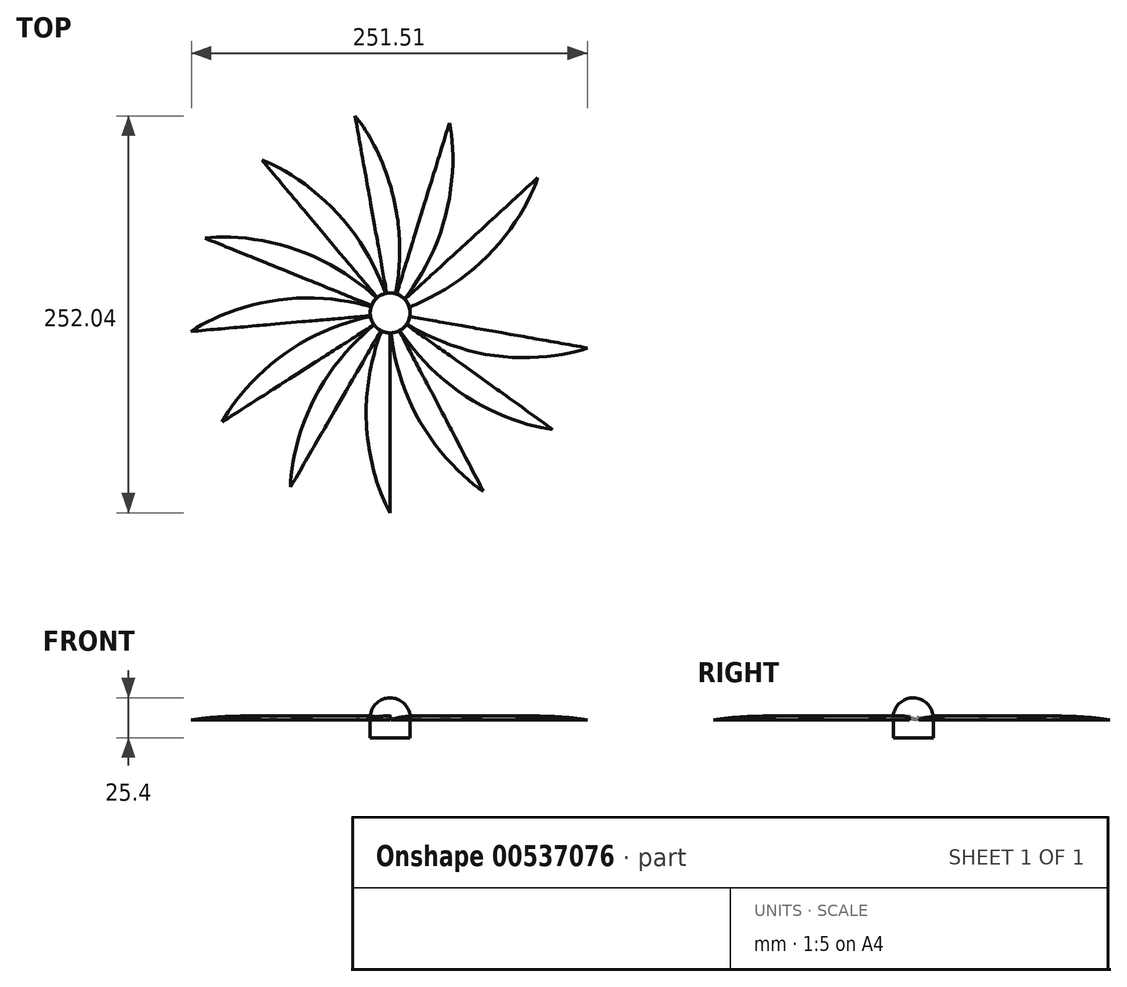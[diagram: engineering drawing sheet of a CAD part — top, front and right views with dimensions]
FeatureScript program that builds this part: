
annotation { "Feature Type Name" : "Feature", "Feature Type Description" : "" }
export const myFeature = defineFeature(function(context is Context, id is Id, definition is map)
    precondition{}
    {
        {
            var Q0;
            Q0=qCreatedBy(makeId("Top.planeOp"),FACE);
            var sketch = newSketch(context, id + "F0", { "sketchPlane" : qUnion([Q0])});
            skCircle(sketch, "E0", {"center": v(0, 0) * mm, "radius": 12.7 * mm});
            skLineSegment(sketch, "E1", {"start": v(0, 0) * mm, "end": v(0, 12.7) * mm});
            skLineSegment(sketch, "E2", {"start": v(0, 0) * mm, "end": v(0, -12.7) * mm});
            skSolve(sketch);
        }
        {
            var Q0;
            {var subQ0=sQuery(id+"F0.wireOp",EDGE,"E1");Q0=makeQuery(id+"F0.imprint","IMPRINT",FACE,{"disambiguationData":[TD([[makeQuery(id+"F0.imprint","IMPRINT",EDGE,{"derivedFrom":subQ0}),-1.0]])]});}
            var Q1;
            Q1=sQuery(id+"F0.wireOp",EDGE,"E1");
            revolve(context, id + "F1", {"entities" : qUnion([Q0]), "axis" : qUnion([Q1]), "revolveType" : RevolveType.FULL});
        }
        {
            var Q0;
            Q0=qCreatedBy(makeId("Top.planeOp"),FACE);
            var sketch = newSketch(context, id + "F2", { "sketchPlane" : qUnion([Q0])});
            skLineSegment(sketch, "E3", {"start": v(0, 0) * mm, "end": v(0, -127) * mm});
            skLineSegment(sketch, "E4", {"start": v(0, 0) * mm, "end": v(0, -63.5) * mm});
            skLineSegment(sketch, "E5", {"start": v(0, 63.5) * mm, "end": v(15.24, 63.5) * mm});
            skLineSegment(sketch, "E6", {"start": v(0, -63.5) * mm, "end": v(-15.24, -63.5) * mm});
            skFitSpline(sketch, "E7", {"points": [v(0, 0) * mm, v(-15.24, -63.5) * mm, v(0, -127) * mm], "startDerivative": vector(-45.72, -76.2) * mm, "endDerivative": vector(45.72, -76.2) * mm});
            skLineSegment(sketch, "E8", {"start": v(0.24, -0.68) * mm, "end": v(59.19, -113.17) * mm});
            skLineSegment(sketch, "E9", {"start": v(0.24, -0.68) * mm, "end": v(29.72, -56.92) * mm});
            skFitSpline(sketch, "E10", {"points": [v(0.24, -0.68) * mm, v(16.22, -64) * mm, v(59.19, -113.17) * mm], "startDerivative": vector(-5.13, -88.72) * mm, "endDerivative": vector(75.86, -46.28) * mm});
            skLineSegment(sketch, "E11", {"start": v(0, 0) * mm, "end": v(103.27, -73.92) * mm});
            skLineSegment(sketch, "E12", {"start": v(0, 0) * mm, "end": v(51.64, -36.96) * mm});
            skFitSpline(sketch, "E13", {"points": [v(0, 0) * mm, v(42.77, -49.35) * mm, v(103.27, -73.92) * mm], "startDerivative": vector(35.35, -81.53) * mm, "endDerivative": vector(88.57, -7.17) * mm});
            skLineSegment(sketch, "E14", {"start": v(0.17, -0.17) * mm, "end": v(125.24, -22.22) * mm});
            skLineSegment(sketch, "E15", {"start": v(0.17, -0.17) * mm, "end": v(62.7, -11.2) * mm});
            skFitSpline(sketch, "E16", {"points": [v(0.17, -0.17) * mm, v(60.06, -26.2) * mm, v(125.24, -22.22) * mm], "startDerivative": vector(70.33, -52.99) * mm, "endDerivative": vector(82.98, 31.8) * mm});
            skLineSegment(sketch, "E17", {"start": v(0.17, -0.17) * mm, "end": v(121.45, 37.53) * mm});
            skFitSpline(sketch, "E18", {"points": [v(0.17, -0.17) * mm, v(65.33, 4.13) * mm, v(121.45, 37.53) * mm], "startDerivative": vector(86.34, -21.04) * mm, "endDerivative": vector(59.2, 66.28) * mm});
            skLineSegment(sketch, "E19", {"start": v(0, 0) * mm, "end": v(93.62, 85.82) * mm});
            skFitSpline(sketch, "E20", {"points": [v(0, 0) * mm, v(57.1, 31.67) * mm, v(93.62, 85.82) * mm], "startDerivative": vector(87.07, 17.79) * mm, "endDerivative": vector(25.28, 85.2) * mm});
            skLineSegment(sketch, "E21", {"start": v(0.24, -0.68) * mm, "end": v(37.6, 120.7) * mm});
            skFitSpline(sketch, "E22", {"points": [v(0.24, -0.68) * mm, v(33.49, 55.53) * mm, v(37.6, 120.7) * mm], "startDerivative": vector(66.11, 59.38) * mm, "endDerivative": vector(-21.28, 86.28) * mm});
            skLineSegment(sketch, "E23", {"start": v(0, 0) * mm, "end": v(-22.24, 125.04) * mm});
            skFitSpline(sketch, "E24", {"points": [v(0, 0) * mm, v(3.88, 65.19) * mm, v(-22.24, 125.04) * mm], "startDerivative": vector(31.67, 83.03) * mm, "endDerivative": vector(-58.36, 67.01) * mm});
            skLineSegment(sketch, "E25", {"start": v(0.17, -0.17) * mm, "end": v(-81.46, 97.12) * mm});
            skFitSpline(sketch, "E26", {"points": [v(0.17, -0.17) * mm, v(-28.97, 58.27) * mm, v(-81.46, 97.12) * mm], "startDerivative": vector(-13.96, 87.76) * mm, "endDerivative": vector(-84, 28.98) * mm});
            skLineSegment(sketch, "E27", {"start": v(0.17, -0.17) * mm, "end": v(-117.57, 47.45) * mm});
            skFitSpline(sketch, "E28", {"points": [v(0.17, -0.17) * mm, v(-52.98, 37.77) * mm, v(-117.57, 47.45) * mm], "startDerivative": vector(-53.5, 70.96) * mm, "endDerivative": vector(-87.78, -13.81) * mm});
            skLineSegment(sketch, "E29", {"start": v(0.24, -0.68) * mm, "end": v(-126.27, -11.74) * mm});
            skFitSpline(sketch, "E30", {"points": [v(0.24, -0.68) * mm, v(-64.34, 8.97) * mm, v(-126.27, -11.74) * mm], "startDerivative": vector(-79.9, 38.9) * mm, "endDerivative": vector(-71.93, -52.19) * mm});
            skLineSegment(sketch, "E31", {"start": v(0.24, -0.68) * mm, "end": v(-106.62, -69.3) * mm});
            skFitSpline(sketch, "E32", {"points": [v(0.24, -0.68) * mm, v(-61.42, -22.16) * mm, v(-106.62, -69.3) * mm], "startDerivative": vector(-88.82, -2.7) * mm, "endDerivative": vector(-39.42, -79.64) * mm});
            skLineSegment(sketch, "E33", {"start": v(0.24, -0.68) * mm, "end": v(-63.26, -110.66) * mm});
            skFitSpline(sketch, "E34", {"points": [v(0.24, -0.68) * mm, v(-44.7, -48.05) * mm, v(-63.26, -110.66) * mm], "startDerivative": vector(-77.7, -43.13) * mm, "endDerivative": vector(1.5, -88.85) * mm});
            skSolve(sketch);
        }
        {
            var Q0;
            {var subQ0=sQuery(id+"F2.wireOp",EDGE,"E4");Q0=makeQuery(id+"F2.imprint","IMPRINT",FACE,{"disambiguationData":[TD([[makeQuery(id+"F2.imprint","IMPRINT",EDGE,{"derivedFrom":subQ0}),-1.0]])]});}
            var Q1;
            {var subQ0=sQuery(id+"F2.wireOp",EDGE,"E3");Q1=makeQuery(id+"F2.imprint","IMPRINT",FACE,{"disambiguationData":[TD([[makeQuery(id+"F2.imprint","IMPRINT",EDGE,{"derivedFrom":subQ0}),-1.0]])]});}
            var Q2;
            {var subQ0=sQuery(id+"F2.wireOp",EDGE,"19Io6KP2-8sqI-wjnz-AJ6c-VTp4O6TYuGnM");Q2=makeQuery(id+"F2.imprint","IMPRINT",FACE,{"disambiguationData":[TD([[makeQuery(id+"F2.imprint","IMPRINT",EDGE,{"derivedFrom":subQ0}),-1.0]])]});}
            var Q3;
            {var subQ0=sQuery(id+"F2.wireOp",EDGE,"X4IT270C-a7Zd-RReP-n4iX-xOcwQeBmdPC1");Q3=makeQuery(id+"F2.imprint","IMPRINT",FACE,{"disambiguationData":[TD([[makeQuery(id+"F2.imprint","IMPRINT",EDGE,{"derivedFrom":subQ0}),-1.0]])]});}
            var Q4;
            {var subQ0=sQuery(id+"F2.wireOp",EDGE,"E6");Q4=makeQuery(id+"F2.imprint","IMPRINT",FACE,{"disambiguationData":[TD([[makeQuery(id+"F2.imprint","IMPRINT",EDGE,{"derivedFrom":subQ0}),-1.0]])]});}
            var Q5;
            {var subQ0=sQuery(id+"F2.wireOp",EDGE,"E33");var subQ1=sQuery(id+"F2.wireOp",EDGE,"E7");var subQ2=makeQuery(id+"F2.imprint","INTERSECT",VERTEX,{"derivedFrom":[subQ1,subQ0]});Q5=makeQuery(id+"F2.imprint","IMPRINT",FACE,{"disambiguationData":[TD([[makeQuery(id+"F2.imprint","IMPRINT",EDGE,{"disambiguationData":[TD([[subQ2,1.0]])],"derivedFrom":subQ1}),-1.0]])]});}
            var Q6;
            {var subQ3=sQuery(id+"F2.wireOp",EDGE,"E29");var subQ7=sQuery(id+"F2.wireOp",EDGE,"E7");var subQ8=makeQuery(id+"F2.imprint","INTERSECT",VERTEX,{"derivedFrom":[subQ7,subQ3]});Q6=makeQuery(id+"F2.imprint","IMPRINT",FACE,{"disambiguationData":[TD([[makeQuery(id+"F2.imprint","IMPRINT",EDGE,{"disambiguationData":[TD([[subQ8,-1.0]])],"derivedFrom":subQ7}),-1.0]])]});}
            var Q7;
            {var subQ0=sQuery(id+"F2.wireOp",EDGE,"E30");var subQ1=sQuery(id+"F2.wireOp",EDGE,"E7");var subQ2=makeQuery(id+"F2.imprint","INTERSECT",VERTEX,{"derivedFrom":[subQ1,subQ0]});Q7=makeQuery(id+"F2.imprint","IMPRINT",FACE,{"disambiguationData":[TD([[makeQuery(id+"F2.imprint","IMPRINT",EDGE,{"disambiguationData":[TD([[subQ2,-1.0]])],"derivedFrom":subQ1}),-1.0]])]});}
            var Q8;
            {var subQ0=sQuery(id+"F2.wireOp",EDGE,"E28");var subQ5=sQuery(id+"F2.wireOp",EDGE,"E25");var subQ6=makeQuery(id+"F2.imprint","INTERSECT",VERTEX,{"derivedFrom":[subQ5,subQ0]});Q8=makeQuery(id+"F2.imprint","IMPRINT",FACE,{"disambiguationData":[TD([[makeQuery(id+"F2.imprint","IMPRINT",EDGE,{"disambiguationData":[TD([[subQ6,1.0]])],"derivedFrom":subQ5}),1.0]])]});}
            var Q9;
            {var subQ0=sQuery(id+"F2.wireOp",EDGE,"E26");var subQ1=sQuery(id+"F2.wireOp",EDGE,"E23");var subQ2=makeQuery(id+"F2.imprint","INTERSECT",VERTEX,{"derivedFrom":[subQ1,subQ0]});Q9=makeQuery(id+"F2.imprint","IMPRINT",FACE,{"disambiguationData":[TD([[makeQuery(id+"F2.imprint","IMPRINT",EDGE,{"disambiguationData":[TD([[subQ2,1.0]])],"derivedFrom":subQ1}),1.0]])]});}
            var Q10;
            {var subQ0=sQuery(id+"F2.wireOp",EDGE,"E24");var subQ1=sQuery(id+"F2.wireOp",EDGE,"E23");var subQ2=makeQuery(id+"F2.imprint","INTERSECT",VERTEX,{"derivedFrom":[subQ1,subQ0]});Q10=makeQuery(id+"F2.imprint","IMPRINT",FACE,{"disambiguationData":[TD([[makeQuery(id+"F2.imprint","IMPRINT",EDGE,{"disambiguationData":[TD([[subQ2,1.0]])],"derivedFrom":subQ1}),-1.0]])]});}
            var Q11;
            {var subQ0=sQuery(id+"F2.wireOp",EDGE,"E21");var subQ1=sQuery(id+"F2.wireOp",EDGE,"E19");var subQ2=makeQuery(id+"F2.imprint","INTERSECT",VERTEX,{"derivedFrom":[subQ1,subQ0]});Q11=makeQuery(id+"F2.imprint","IMPRINT",FACE,{"disambiguationData":[TD([[makeQuery(id+"F2.imprint","IMPRINT",EDGE,{"disambiguationData":[TD([[subQ2,-1.0]])],"derivedFrom":subQ1}),1.0]])]});}
            var Q12;
            {var subQ0=sQuery(id+"F2.wireOp",EDGE,"E20");var subQ1=sQuery(id+"F2.wireOp",EDGE,"E17");var subQ8=makeQuery(id+"F2.imprint","INTERSECT",VERTEX,{"disambiguationData":[OD(0.0)],"derivedFrom":[subQ1,subQ0]});Q12=makeQuery(id+"F2.imprint","IMPRINT",FACE,{"disambiguationData":[TD([[makeQuery(id+"F2.imprint","IMPRINT",EDGE,{"disambiguationData":[TD([[subQ8,1.0]])],"derivedFrom":subQ1}),1.0]])]});}
            var Q13;
            {var subQ0=sQuery(id+"F2.wireOp",EDGE,"E18");var subQ3=sQuery(id+"F2.wireOp",EDGE,"E15");var subQ4=makeQuery(id+"F2.imprint","INTERSECT",VERTEX,{"derivedFrom":[subQ3,subQ0]});Q13=makeQuery(id+"F2.imprint","IMPRINT",FACE,{"disambiguationData":[TD([[makeQuery(id+"F2.imprint","IMPRINT",EDGE,{"disambiguationData":[TD([[subQ4,1.0]])],"derivedFrom":subQ3}),1.0]])]});}
            var Q14;
            {var subQ1=sQuery(id+"F2.wireOp",EDGE,"E14");Q14=makeQuery(id+"F2.imprint","IMPRINT",FACE,{"disambiguationData":[TD([[makeQuery(id+"F2.imprint","IMPRINT",EDGE,{"derivedFrom":subQ1}),-1.0]])]});}
            var Q15;
            {var subQ9=sQuery(id+"F2.wireOp",EDGE,"E11");Q15=makeQuery(id+"F2.imprint","IMPRINT",FACE,{"disambiguationData":[TD([[makeQuery(id+"F2.imprint","IMPRINT",EDGE,{"derivedFrom":subQ9}),-1.0]])]});}
            var Q16;
            {var subQ2=sQuery(id+"F2.wireOp",EDGE,"E8");Q16=makeQuery(id+"F2.imprint","IMPRINT",FACE,{"disambiguationData":[TD([[makeQuery(id+"F2.imprint","IMPRINT",EDGE,{"derivedFrom":subQ2}),-1.0]])]});}
            extrude(context, id + "F3", {"entities" : qUnion([Q0, Q1, Q2, Q3, Q4, Q5, Q6, Q7, Q8, Q9, Q10, Q11, Q12, Q13, Q14, Q15, Q16]), "operationType" : NewBodyOperationType.ADD, "depth" : 2.54 * mm, "offsetDistance" : 25.4 * mm, "symmetric" : true});
        }
        {
            var Q0;
            Q0=makeQuery(id+"F3.opExtrude","CAP_EDGE",EDGE,{"disambiguationData":[OSD([sQuery(id+"F2.wireOp",EDGE,"0b77368a-5ada-40fb-88a0-015b6c9d9cfb")])],"isStart":false});
            var Q1;
            Q1=makeQuery(id+"F3.opExtrude","CAP_EDGE",EDGE,{"disambiguationData":[OSD([sQuery(id+"F2.wireOp",EDGE,"E7")])],"isStart":false});
            var Q2;
            {var subQ0=sQuery(id+"F2.wireOp",EDGE,"E34");Q2=makeQuery(id+"F3.opExtrude","CAP_EDGE",EDGE,{"disambiguationData":[OSD([subQ0]),TDD([makeQuery(id+"F2.imprint","IMPRINT",EDGE,{"disambiguationData":[TD([[makeQuery(id+"F2.imprint","INTERSECT",VERTEX,{"derivedFrom":[sQuery(id+"F2.wireOp",EDGE,"E33"),subQ0]}),1.0]])],"derivedFrom":subQ0})])],"isStart":false});}
            var Q3;
            {var subQ0=sQuery(id+"F2.wireOp",EDGE,"E32");Q3=makeQuery(id+"F3.opExtrude","CAP_EDGE",EDGE,{"disambiguationData":[OSD([subQ0]),TDD([makeQuery(id+"F2.imprint","IMPRINT",EDGE,{"disambiguationData":[TD([[makeQuery(id+"F2.imprint","INTERSECT",VERTEX,{"derivedFrom":[sQuery(id+"F2.wireOp",EDGE,"E31"),subQ0]}),1.0]])],"derivedFrom":subQ0})])],"isStart":false});}
            var Q4;
            Q4=makeQuery(id+"F3.opExtrude","CAP_EDGE",EDGE,{"disambiguationData":[OSD([sQuery(id+"F2.wireOp",EDGE,"E30")])],"isStart":false});
            var Q5;
            {var subQ0=sQuery(id+"F2.wireOp",EDGE,"E28");Q5=makeQuery(id+"F3.opExtrude","CAP_EDGE",EDGE,{"disambiguationData":[OSD([subQ0]),TDD([makeQuery(id+"F2.imprint","IMPRINT",EDGE,{"disambiguationData":[TD([[makeQuery(id+"F2.imprint","INTERSECT",VERTEX,{"derivedFrom":[sQuery(id+"F2.wireOp",EDGE,"E27"),subQ0]}),1.0]])],"derivedFrom":subQ0})])],"isStart":false});}
            var Q6;
            {var subQ0=sQuery(id+"F2.wireOp",EDGE,"E26");Q6=makeQuery(id+"F3.opExtrude","CAP_EDGE",EDGE,{"disambiguationData":[OSD([subQ0]),TDD([makeQuery(id+"F2.imprint","IMPRINT",EDGE,{"disambiguationData":[TD([[makeQuery(id+"F2.imprint","INTERSECT",VERTEX,{"derivedFrom":[sQuery(id+"F2.wireOp",EDGE,"E25"),subQ0]}),1.0]])],"derivedFrom":subQ0})])],"isStart":false});}
            var Q7;
            Q7=makeQuery(id+"F3.opExtrude","CAP_EDGE",EDGE,{"disambiguationData":[OSD([sQuery(id+"F2.wireOp",EDGE,"E24")])],"isStart":false});
            var Q8;
            {var subQ0=sQuery(id+"F2.wireOp",EDGE,"E22");Q8=makeQuery(id+"F3.opExtrude","CAP_EDGE",EDGE,{"disambiguationData":[OSD([subQ0]),TDD([makeQuery(id+"F2.imprint","IMPRINT",EDGE,{"disambiguationData":[TD([[makeQuery(id+"F2.imprint","INTERSECT",VERTEX,{"derivedFrom":[sQuery(id+"F2.wireOp",EDGE,"E21"),subQ0]}),1.0]])],"derivedFrom":subQ0})])],"isStart":false});}
            var Q9;
            {var subQ0=sQuery(id+"F2.wireOp",EDGE,"E20");Q9=makeQuery(id+"F3.opExtrude","CAP_EDGE",EDGE,{"disambiguationData":[OSD([subQ0]),TDD([makeQuery(id+"F2.imprint","IMPRINT",EDGE,{"disambiguationData":[TD([[makeQuery(id+"F2.imprint","INTERSECT",VERTEX,{"derivedFrom":[sQuery(id+"F2.wireOp",EDGE,"E19"),subQ0]}),1.0]])],"derivedFrom":subQ0})])],"isStart":false});}
            var Q10;
            {var subQ0=sQuery(id+"F2.wireOp",EDGE,"E18");Q10=makeQuery(id+"F3.opExtrude","CAP_EDGE",EDGE,{"disambiguationData":[OSD([subQ0]),TDD([makeQuery(id+"F2.imprint","IMPRINT",EDGE,{"disambiguationData":[TD([[makeQuery(id+"F2.imprint","INTERSECT",VERTEX,{"derivedFrom":[sQuery(id+"F2.wireOp",EDGE,"E17"),subQ0]}),1.0]])],"derivedFrom":subQ0})])],"isStart":false});}
            var Q11;
            {var subQ0=sQuery(id+"F2.wireOp",EDGE,"E16");Q11=makeQuery(id+"F3.opExtrude","CAP_EDGE",EDGE,{"disambiguationData":[OSD([subQ0]),TDD([makeQuery(id+"F2.imprint","IMPRINT",EDGE,{"disambiguationData":[TD([[makeQuery(id+"F2.imprint","INTERSECT",VERTEX,{"derivedFrom":[sQuery(id+"F2.wireOp",EDGE,"E14"),subQ0]}),1.0]])],"derivedFrom":subQ0})])],"isStart":false});}
            var Q12;
            {var subQ0=sQuery(id+"F2.wireOp",EDGE,"E13");Q12=makeQuery(id+"F3.opExtrude","CAP_EDGE",EDGE,{"disambiguationData":[OSD([subQ0]),TDD([makeQuery(id+"F2.imprint","IMPRINT",EDGE,{"disambiguationData":[TD([[makeQuery(id+"F2.imprint","INTERSECT",VERTEX,{"derivedFrom":[sQuery(id+"F2.wireOp",EDGE,"E11"),subQ0]}),1.0]])],"derivedFrom":subQ0})])],"isStart":false});}
            var Q13;
            Q13=makeQuery(id+"F3.opExtrude","CAP_EDGE",EDGE,{"disambiguationData":[OSD([sQuery(id+"F2.wireOp",EDGE,"E10")])],"isStart":false});
            fillet(context, id + "F4", {"entities" : qUnion([Q0, Q1, Q2, Q3, Q4, Q5, Q6, Q7, Q8, Q9, Q10, Q11, Q12, Q13]), "radius" : 45.72 * mm, "tangentPropagation" : true, "rho" : 0.5, "crossSection" : FilletCrossSection.CONIC, "allowEdgeOverflow" : false});
        }
        {
            var Q0;
            Q0=qCreatedBy(makeId("Top.planeOp"),FACE);
            var sketch = newSketch(context, id + "F5", { "sketchPlane" : qUnion([Q0])});
            skCircle(sketch, "E35", {"center": v(0, 0) * mm, "radius": 12.7 * mm});
            skSolve(sketch);
        }
        {
            var Q0;
            Q0=makeQuery(id+"F5.imprint","IMPRINT",FACE,{"disambiguationData":[TD([[makeQuery(id+"F5.imprint","IMPRINT",EDGE,{"derivedFrom":sQuery(id+"F5.wireOp",EDGE,"E35")}),1.0]])]});
            extrude(context, id + "F6", {"entities" : qUnion([Q0]), "operationType" : NewBodyOperationType.ADD, "oppositeDirection" : true, "depth" : 12.7 * mm, "offsetDistance" : 25.4 * mm});
        }
    });
